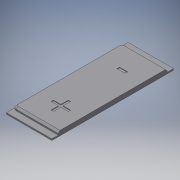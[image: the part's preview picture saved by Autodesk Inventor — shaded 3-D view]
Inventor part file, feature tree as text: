
AUTODESK INVENTOR PART (.ipt)
format: ipt  version: 2016 SP2 (Build 200236200, 236)  size: 172,032 bytes
history: native  units: mm
features: sketch x4, other x3
ambient origin geometry x8: Origin, YZ Plane, XZ Plane, XY Plane, X Axis, Y Axis, Z Axis, Center Point
bodies: Volumenkörper1 (feature_tree)
feature tree (7):
  other  "Button.ipt"
  other  "Volumenkörper1::Button.ipt"
  other  "Bezeichnung1"
  sketch  "Skizze1"  dims[d0=10.0mm]
  sketch  "Skizze2"
  sketch  "Skizze3"
  sketch  "Skizze4"
